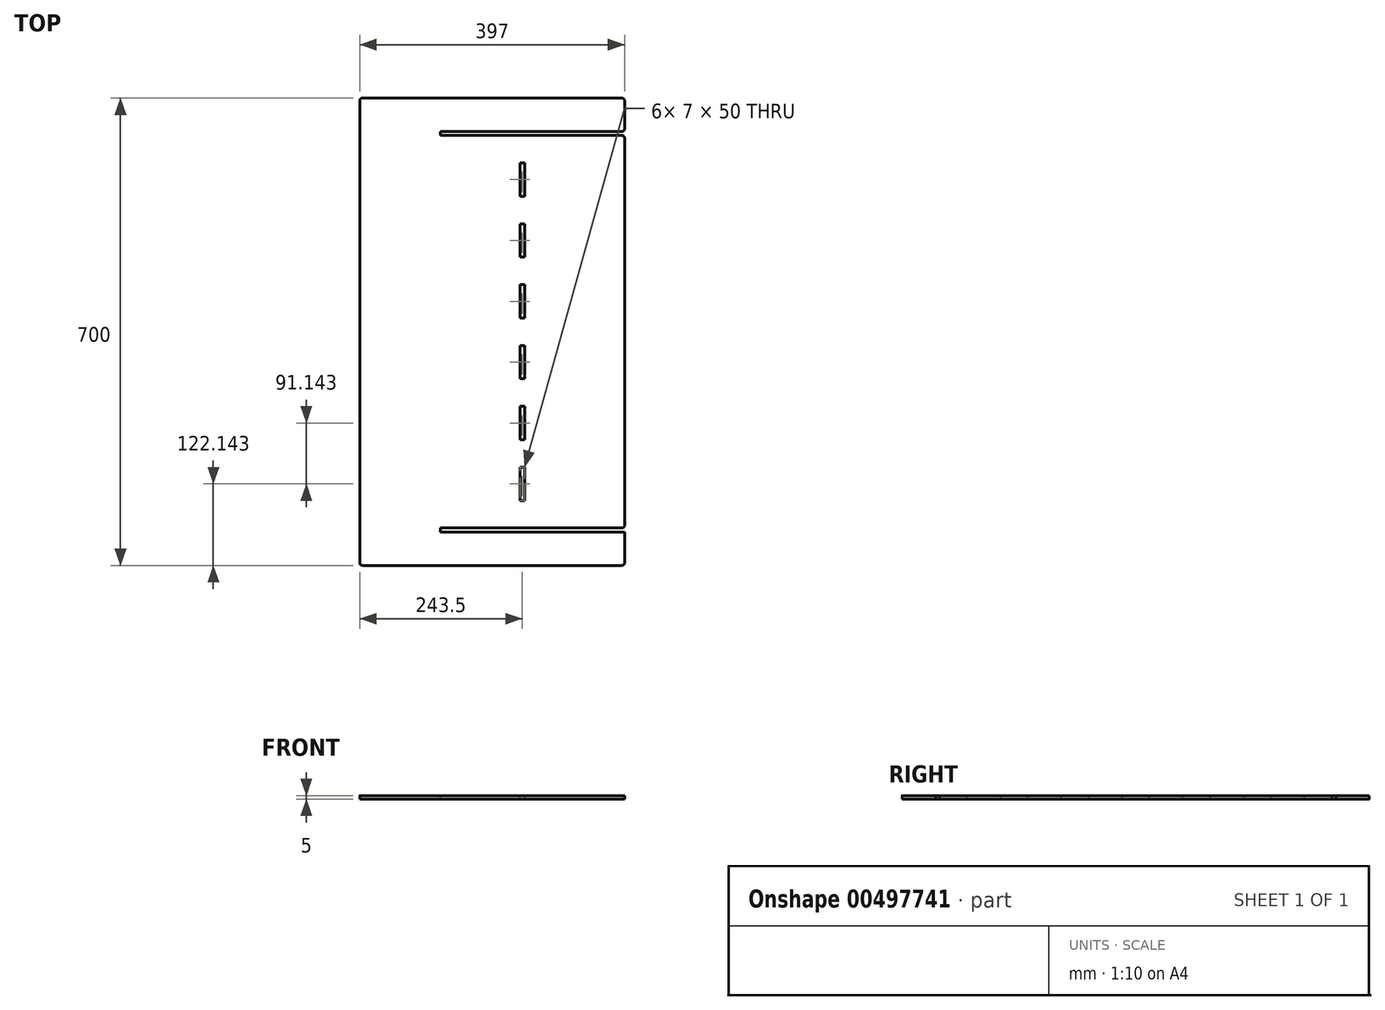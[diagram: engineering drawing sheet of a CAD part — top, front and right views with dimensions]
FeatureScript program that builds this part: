
annotation { "Feature Type Name" : "Feature", "Feature Type Description" : "" }
export const myFeature = defineFeature(function(context is Context, id is Id, definition is map)
    precondition{}
    {
        {
            var Q0;
            Q0=qCreatedBy(makeId("Top.planeOp"),FACE);
            var sketch = newSketch(context, id + "F0", { "sketchPlane" : qUnion([Q0])});
            skLineSegment(sketch, "E0.bottom", {"start": v(198.5, -350) * mm, "end": v(-198.5, -350) * mm});
            skLineSegment(sketch, "E0.top", {"start": v(198.5, 350) * mm, "end": v(-198.5, 350) * mm});
            skLineSegment(sketch, "E0.left", {"start": v(198.5, -350) * mm, "end": v(198.5, 350) * mm});
            skLineSegment(sketch, "E0.right", {"start": v(-198.5, -350) * mm, "end": v(-198.5, 350) * mm});
            skPoint(sketch, "E0.middle", {"position": v(0, 0) * mm});
            skSolve(sketch);
        }
        {
            var Q0;
            Q0 = qSketchRegion(id + "F0", true);
            extrude(context, id + "F1", {"entities" : qUnion([Q0]), "depth" : 5 * mm, "offsetDistance" : 25 * mm});
        }
        {
            var Q0;
            Q0=makeQuery(id+"F1.opExtrude","CAP_FACE",FACE,{"disambiguationData":[OSD([sQuery(id+"F0.wireOp",EDGE,"E0.bottom"),sQuery(id+"F0.wireOp",EDGE,"E0.top"),sQuery(id+"F0.wireOp",EDGE,"E0.left"),sQuery(id+"F0.wireOp",EDGE,"E0.right")])],"isStart":false});
            var sketch = newSketch(context, id + "F2", { "sketchPlane" : qUnion([Q0])});
            skLineSegment(sketch, "E1.bottom", {"start": v(198.5, -300) * mm, "end": v(-77.5, -300) * mm});
            skLineSegment(sketch, "E1.top", {"start": v(198.5, -294) * mm, "end": v(-77.5, -294) * mm});
            skLineSegment(sketch, "E1.left", {"start": v(198.5, -300) * mm, "end": v(198.5, -294) * mm});
            skLineSegment(sketch, "E1.right", {"start": v(-77.5, -300) * mm, "end": v(-77.5, -294) * mm});
            skLineSegment(sketch, "E2.bottom", {"start": v(198.5, 300) * mm, "end": v(-77.5, 300) * mm});
            skLineSegment(sketch, "E2.top", {"start": v(198.5, 294) * mm, "end": v(-77.5, 294) * mm});
            skLineSegment(sketch, "E2.left", {"start": v(198.5, 300) * mm, "end": v(198.5, 294) * mm});
            skLineSegment(sketch, "E2.right", {"start": v(-77.5, 300) * mm, "end": v(-77.5, 294) * mm});
            skLineSegment(sketch, "E3", {"start": v(198.5, -350) * mm, "end": v(198.5, -300) * mm, "construction": true});
            skLineSegment(sketch, "E4", {"start": v(198.5, 350) * mm, "end": v(198.5, 300) * mm, "construction": true});
            skSolve(sketch);
        }
        {
            var Q0;
            Q0 = qSketchRegion(id + "F2", true);
            extrude(context, id + "F3", {"entities" : qUnion([Q0]), "operationType" : NewBodyOperationType.REMOVE, "oppositeDirection" : true, "depth" : 25 * mm});
        }
        {
            var Q0;
            Q0=makeQuery(id+"F1.opExtrude","CAP_FACE",FACE,{"disambiguationData":[OSD([sQuery(id+"F0.wireOp",EDGE,"E0.bottom"),sQuery(id+"F0.wireOp",EDGE,"E0.top"),sQuery(id+"F0.wireOp",EDGE,"E0.left"),sQuery(id+"F0.wireOp",EDGE,"E0.right")])],"isStart":false});
            var sketch = newSketch(context, id + "F4", { "sketchPlane" : qUnion([Q0])});
            skLineSegment(sketch, "E5.bottom", {"start": v(41.5, 161.71) * mm, "end": v(48.5, 161.71) * mm});
            skLineSegment(sketch, "E5.top", {"start": v(41.5, 111.71) * mm, "end": v(48.5, 111.71) * mm});
            skLineSegment(sketch, "E5.left", {"start": v(41.5, 161.71) * mm, "end": v(41.5, 111.71) * mm});
            skLineSegment(sketch, "E5.right", {"start": v(48.5, 161.71) * mm, "end": v(48.5, 111.71) * mm});
            skLineSegment(sketch, "E6.bottom", {"start": v(41.5, 70.57) * mm, "end": v(48.5, 70.57) * mm});
            skLineSegment(sketch, "E6.top", {"start": v(41.5, 20.57) * mm, "end": v(48.5, 20.57) * mm});
            skLineSegment(sketch, "E6.left", {"start": v(41.5, 70.57) * mm, "end": v(41.5, 20.57) * mm});
            skLineSegment(sketch, "E6.right", {"start": v(48.5, 70.57) * mm, "end": v(48.5, 20.57) * mm});
            skLineSegment(sketch, "E7.bottom", {"start": v(41.5, -20.57) * mm, "end": v(48.5, -20.57) * mm});
            skLineSegment(sketch, "E7.top", {"start": v(41.5, -70.57) * mm, "end": v(48.5, -70.57) * mm});
            skLineSegment(sketch, "E7.left", {"start": v(41.5, -20.57) * mm, "end": v(41.5, -70.57) * mm});
            skLineSegment(sketch, "E7.right", {"start": v(48.5, -20.57) * mm, "end": v(48.5, -70.57) * mm});
            skLineSegment(sketch, "E8.bottom", {"start": v(41.5, -111.71) * mm, "end": v(48.5, -111.71) * mm});
            skLineSegment(sketch, "E8.top", {"start": v(41.5, -161.71) * mm, "end": v(48.5, -161.71) * mm});
            skLineSegment(sketch, "E8.left", {"start": v(41.5, -111.71) * mm, "end": v(41.5, -161.71) * mm});
            skLineSegment(sketch, "E8.right", {"start": v(48.5, -111.71) * mm, "end": v(48.5, -161.71) * mm});
            skLineSegment(sketch, "E9.bottom", {"start": v(41.5, -202.86) * mm, "end": v(48.5, -202.86) * mm});
            skLineSegment(sketch, "E9.top", {"start": v(41.5, -252.86) * mm, "end": v(48.5, -252.86) * mm});
            skLineSegment(sketch, "E9.left", {"start": v(41.5, -202.86) * mm, "end": v(41.5, -252.86) * mm});
            skLineSegment(sketch, "E9.right", {"start": v(48.5, -202.86) * mm, "end": v(48.5, -252.86) * mm});
            skLineSegment(sketch, "E10.bottom", {"start": v(41.5, 252.86) * mm, "end": v(48.5, 252.86) * mm});
            skLineSegment(sketch, "E10.top", {"start": v(41.5, 202.86) * mm, "end": v(48.5, 202.86) * mm});
            skLineSegment(sketch, "E10.left", {"start": v(41.5, 252.86) * mm, "end": v(41.5, 202.86) * mm});
            skLineSegment(sketch, "E10.right", {"start": v(48.5, 252.86) * mm, "end": v(48.5, 202.86) * mm});
            skLineSegment(sketch, "E11", {"start": v(48.5, 202.86) * mm, "end": v(48.5, 161.71) * mm, "construction": true});
            skLineSegment(sketch, "E12", {"start": v(48.5, 111.71) * mm, "end": v(48.5, 70.57) * mm, "construction": true});
            skLineSegment(sketch, "E13", {"start": v(48.5, 20.57) * mm, "end": v(48.5, -20.57) * mm, "construction": true});
            skLineSegment(sketch, "E14", {"start": v(48.5, -70.57) * mm, "end": v(48.5, -111.71) * mm, "construction": true});
            skLineSegment(sketch, "E15", {"start": v(48.5, -161.71) * mm, "end": v(48.5, -202.86) * mm, "construction": true});
            skLineSegment(sketch, "E16", {"start": v(48.5, 252.86) * mm, "end": v(48.5, 294) * mm, "construction": true});
            skLineSegment(sketch, "E17", {"start": v(48.5, -252.86) * mm, "end": v(48.5, -294) * mm, "construction": true});
            skSolve(sketch);
        }
        {
            var Q0;
            Q0=makeQuery(id+"F4.imprint","IMPRINT",FACE,{"disambiguationData":[TD([[makeQuery(id+"F4.imprint","IMPRINT",EDGE,{"derivedFrom":sQuery(id+"F4.wireOp",EDGE,"E6.bottom")}),-1.0]])]});
            var Q1;
            Q1=makeQuery(id+"F4.imprint","IMPRINT",FACE,{"disambiguationData":[TD([[makeQuery(id+"F4.imprint","IMPRINT",EDGE,{"derivedFrom":sQuery(id+"F4.wireOp",EDGE,"E5.bottom")}),-1.0]])]});
            var Q2;
            Q2=makeQuery(id+"F4.imprint","IMPRINT",FACE,{"disambiguationData":[TD([[makeQuery(id+"F4.imprint","IMPRINT",EDGE,{"derivedFrom":sQuery(id+"F4.wireOp",EDGE,"E10.bottom")}),-1.0]])]});
            var Q3;
            Q3=makeQuery(id+"F4.imprint","IMPRINT",FACE,{"disambiguationData":[TD([[makeQuery(id+"F4.imprint","IMPRINT",EDGE,{"derivedFrom":sQuery(id+"F4.wireOp",EDGE,"E7.bottom")}),-1.0]])]});
            var Q4;
            Q4=makeQuery(id+"F4.imprint","IMPRINT",FACE,{"disambiguationData":[TD([[makeQuery(id+"F4.imprint","IMPRINT",EDGE,{"derivedFrom":sQuery(id+"F4.wireOp",EDGE,"E8.bottom")}),-1.0]])]});
            var Q5;
            Q5=makeQuery(id+"F4.imprint","IMPRINT",FACE,{"disambiguationData":[TD([[makeQuery(id+"F4.imprint","IMPRINT",EDGE,{"derivedFrom":sQuery(id+"F4.wireOp",EDGE,"E9.bottom")}),-1.0]])]});
            extrude(context, id + "F5", {"entities" : qUnion([Q0, Q1, Q2, Q3, Q4, Q5]), "operationType" : NewBodyOperationType.REMOVE, "oppositeDirection" : true, "depth" : 25 * mm});
        }
        {
            var Q0;
            Q0=makeQuery(id+"F1.opExtrude","SWEPT_EDGE",EDGE,{"disambiguationData":[OSD([sQuery(id+"F0.wireOp",EDGE,"E0.bottom"),sQuery(id+"F0.wireOp",EDGE,"E0.right")])]});
            var Q1;
            Q1=makeQuery(id+"F1.opExtrude","SWEPT_EDGE",EDGE,{"disambiguationData":[OSD([sQuery(id+"F0.wireOp",EDGE,"E0.bottom"),sQuery(id+"F0.wireOp",EDGE,"E0.left")])]});
            var Q2;
            Q2=makeQuery(id+"F3.boolean.opBoolean","COPY",EDGE,{"derivedFrom":makeQuery(id+"F3.opExtrude","SWEPT_EDGE",EDGE,{"disambiguationData":[OSD([sQuery(id+"F0.wireOp",EDGE,"E0.left"),sQuery(id+"F2.wireOp",EDGE,"E1.bottom"),sQuery(id+"F2.wireOp",EDGE,"E1.left")])]})});
            var Q3;
            Q3=makeQuery(id+"F3.boolean.opBoolean","COPY",EDGE,{"derivedFrom":makeQuery(id+"F3.opExtrude","SWEPT_EDGE",EDGE,{"disambiguationData":[OSD([sQuery(id+"F0.wireOp",EDGE,"E0.left"),sQuery(id+"F2.wireOp",EDGE,"E1.top"),sQuery(id+"F2.wireOp",EDGE,"E1.left")])]})});
            var Q4;
            Q4=makeQuery(id+"F3.boolean.opBoolean","COPY",EDGE,{"derivedFrom":makeQuery(id+"F3.opExtrude","SWEPT_EDGE",EDGE,{"disambiguationData":[OSD([sQuery(id+"F0.wireOp",EDGE,"E0.left"),sQuery(id+"F2.wireOp",EDGE,"E2.top"),sQuery(id+"F2.wireOp",EDGE,"E2.left")])]})});
            var Q5;
            Q5=makeQuery(id+"F3.boolean.opBoolean","COPY",EDGE,{"derivedFrom":makeQuery(id+"F3.opExtrude","SWEPT_EDGE",EDGE,{"disambiguationData":[OSD([sQuery(id+"F0.wireOp",EDGE,"E0.left"),sQuery(id+"F2.wireOp",EDGE,"E2.bottom"),sQuery(id+"F2.wireOp",EDGE,"E2.left")])]})});
            var Q6;
            Q6=makeQuery(id+"F1.opExtrude","SWEPT_EDGE",EDGE,{"disambiguationData":[OSD([sQuery(id+"F0.wireOp",EDGE,"E0.top"),sQuery(id+"F0.wireOp",EDGE,"E0.left")])]});
            var Q7;
            Q7=makeQuery(id+"F1.opExtrude","SWEPT_EDGE",EDGE,{"disambiguationData":[OSD([sQuery(id+"F0.wireOp",EDGE,"E0.top"),sQuery(id+"F0.wireOp",EDGE,"E0.right")])]});
            fillet(context, id + "F6", {"entities" : qUnion([Q0, Q1, Q2, Q3, Q4, Q5, Q6, Q7]), "radius" : 4 * mm, "tangentPropagation" : true, "allowEdgeOverflow" : false});
        }
    });
